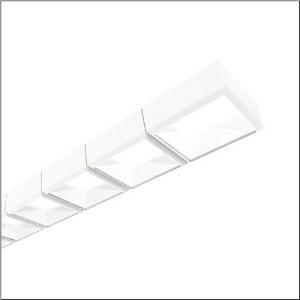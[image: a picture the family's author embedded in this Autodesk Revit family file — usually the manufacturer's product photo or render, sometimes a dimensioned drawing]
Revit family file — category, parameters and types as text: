
# Revit family: scriptus_11_5mz314d04wa
name_source: partatom
category: Lighting Fixtures
units: mm (PartAtom-declared; Revit-internal decimal feet)

## family parameters
Cut with Voids When Loaded = No
Host = Face
Light Source = No
Part Type = Normal
Room Calculation Point = No
Round Connector Dimension = Use Diameter
Shared = No

## types (1)
- Scriptus 11 (1 x LED 4000K / CRI = 80 (unbekannt), 3220 lm / 4820 lm, 4000K)
    Apparent Load = 120 VA
    CIE Flux Codes = - - - 0 100 / 82 95 99 100 100
    Color Rendering = 80
    Color Temperature = 4000K
    Default Elevation = 1800 mm
    Description = Scriptus 11, office luminaire, primary optical cover: lenses, CAT 2 (L<= 3000cd/m²), light emission: direct/indirect distribution, primary light characteristic: symmetric, installation type: suspended mounting, LED, rated luminous flux: 16.060lm, luminous efficacy: 133lm/W, light colour: 840, colour temperature: 4000K, control gear: DALI, with terminal, 5-pole, mains connection: 230V, AC, 50Hz, rated input power: 120W, LED, control gear: ECG DALI, housing, luminaire housing, of aluminium, traffic white (RAL 9016), length: 3.088mm, width: 114mm, height: 57mm, protection rating (complete): IP20, insulation class (complete): insulation class I (protective earthing), certification: CE, ENEC, VDE, protection symbol: F, permissible operating ambient temperature: 0..+35°C, standard: EN 50419, packaging unit: 1 piece
    Height = 57 mm
    Lamp = 1 x LED 4000K / CRI >= 80 (unbekannt)
    Lamp Light Flux = 3220 lm / 4820 lm
    Lamp count = 1
    Length = 3088 mm
    Luminous efficacy = 134 lm/W
    Manufacturer = Siteco
    ModVariant = No
    Model = 5MZ314D04WA
    Mounting Place = Ceiling
    Mounting Type = Pendant
    Number of Poles = 1
    OnlyDefault = Yes
    Power Factor = 1
    Product Name = Scriptus 11
    Product group = office luminaire | ceiling pendant
    ProductGroupID = 903
    Protection Class = Protection class I
    Protection Degree = IP 20
    RLX_Detail_Level = 1
    RLX_Emergency_Light_Flux = 0 lm
    RLX_Emergency_Type = 0
    RLX_Emergency_Type_DB = No
    RlxData = <blob elided: 31905 chars, md5=994df191>
    Socket = socket
    Standby Power = 0 W
    System Light Flux = 16080 lm
    System Power = 120 W
    Type Comments = Product without accessories
    Type Image = l_1004839.jpg
    URL = http://relux.com
    VarID = ---
    Voltage = 0 V
    Weight = 0.00 kg
    Width = 114 mm

## geometry (parser evidence)
native form markers: Blend x4, Sweep x23
no freeform markers — native parametric forms only
